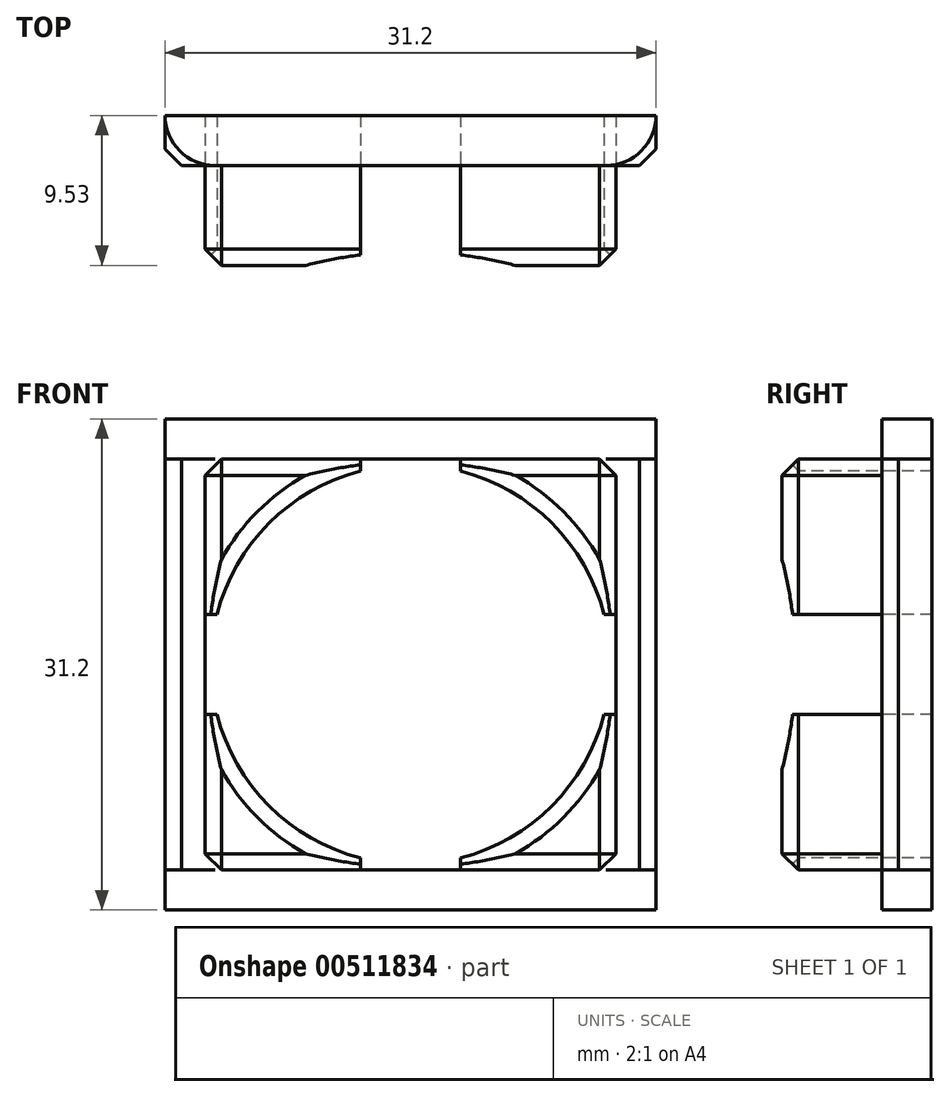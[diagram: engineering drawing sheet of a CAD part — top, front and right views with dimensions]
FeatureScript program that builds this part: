
annotation { "Feature Type Name" : "Feature", "Feature Type Description" : "" }
export const myFeature = defineFeature(function(context is Context, id is Id, definition is map)
    precondition{}
    {
        {
            var Q0;
            Q0=qCreatedBy(makeId("Front.planeOp"),FACE);
            var sketch = newSketch(context, id + "F0", { "sketchPlane" : qUnion([Q0])});
            skLineSegment(sketch, "E0.bottom", {"start": v(-15.6, 15.6) * mm, "end": v(15.6, 15.6) * mm});
            skLineSegment(sketch, "E0.top", {"start": v(-15.6, -15.6) * mm, "end": v(15.6, -15.6) * mm});
            skLineSegment(sketch, "E0.left", {"start": v(-15.6, 15.6) * mm, "end": v(-15.6, -15.6) * mm});
            skLineSegment(sketch, "E0.right", {"start": v(15.6, 15.6) * mm, "end": v(15.6, -15.6) * mm});
            skLineSegment(sketch, "E1", {"start": v(-15.6, 15.6) * mm, "end": v(15.6, -15.6) * mm, "construction": true});
            skLineSegment(sketch, "E2.0", {"start": v(-13.06, 13.06) * mm, "end": v(13.06, 13.06) * mm});
            skLineSegment(sketch, "E2.1", {"start": v(-13.06, 13.06) * mm, "end": v(-13.06, -13.06) * mm});
            skLineSegment(sketch, "E2.2", {"start": v(-13.06, -13.06) * mm, "end": v(13.06, -13.06) * mm});
            skLineSegment(sketch, "E2.3", {"start": v(13.06, 13.06) * mm, "end": v(13.06, -13.06) * mm});
            skCircle(sketch, "E3", {"center": v(0, 0) * mm, "radius": 12.7 * mm});
            skLineSegment(sketch, "E4", {"start": v(0, 13.06) * mm, "end": v(0, -13.06) * mm, "construction": true});
            skLineSegment(sketch, "E5", {"start": v(13.06, 0) * mm, "end": v(-13.06, 0) * mm, "construction": true});
            skLineSegment(sketch, "E6.0", {"start": v(-3.17, 13.06) * mm, "end": v(-3.17, -13.06) * mm});
            skLineSegment(sketch, "E7.MirrorCS", {"start": v(3.17, 13.06) * mm, "end": v(3.17, -13.06) * mm});
            skLineSegment(sketch, "E8.0", {"start": v(13.06, 3.18) * mm, "end": v(-13.06, 3.17) * mm});
            skLineSegment(sketch, "E9.MirrorCS", {"start": v(13.06, -3.18) * mm, "end": v(-13.06, -3.18) * mm});
            skSolve(sketch);
        }
        {
            var Q0;
            Q0=makeQuery(id+"F0.imprint","IMPRINT",FACE,{"disambiguationData":[TD([[makeQuery(id+"F0.imprint","IMPRINT",EDGE,{"derivedFrom":sQuery(id+"F0.wireOp",EDGE,"E0.bottom")}),-1.0]])]});
            var Q1;
            {var subQ0=sQuery(id+"F0.wireOp",EDGE,"E2.3");var subQ1=sQuery(id+"F0.wireOp",EDGE,"E2.0");var subQ2=makeQuery(id+"F0.imprint","INTERSECT",VERTEX,{"derivedFrom":[subQ1,subQ0]});Q1=makeQuery(id+"F0.imprint","IMPRINT",FACE,{"disambiguationData":[TD([[makeQuery(id+"F0.imprint","IMPRINT",EDGE,{"disambiguationData":[TD([[subQ2,1.0]])],"derivedFrom":subQ1}),-1.0]])]});}
            var Q2;
            {var subQ0=sQuery(id+"F0.wireOp",EDGE,"E2.1");var subQ1=sQuery(id+"F0.wireOp",EDGE,"E2.0");var subQ2=makeQuery(id+"F0.imprint","INTERSECT",VERTEX,{"derivedFrom":[subQ1,subQ0]});Q2=makeQuery(id+"F0.imprint","IMPRINT",FACE,{"disambiguationData":[TD([[makeQuery(id+"F0.imprint","IMPRINT",EDGE,{"disambiguationData":[TD([[subQ2,-1.0]])],"derivedFrom":subQ1}),-1.0]])]});}
            var Q3;
            {var subQ0=sQuery(id+"F0.wireOp",EDGE,"E2.2");var subQ1=sQuery(id+"F0.wireOp",EDGE,"E2.1");var subQ2=makeQuery(id+"F0.imprint","INTERSECT",VERTEX,{"derivedFrom":[subQ1,subQ0]});Q3=makeQuery(id+"F0.imprint","IMPRINT",FACE,{"disambiguationData":[TD([[makeQuery(id+"F0.imprint","IMPRINT",EDGE,{"disambiguationData":[TD([[subQ2,1.0]])],"derivedFrom":subQ1}),1.0]])]});}
            var Q4;
            {var subQ0=sQuery(id+"F0.wireOp",EDGE,"E2.3");var subQ1=sQuery(id+"F0.wireOp",EDGE,"E2.2");var subQ2=makeQuery(id+"F0.imprint","INTERSECT",VERTEX,{"derivedFrom":[subQ1,subQ0]});Q4=makeQuery(id+"F0.imprint","IMPRINT",FACE,{"disambiguationData":[TD([[makeQuery(id+"F0.imprint","IMPRINT",EDGE,{"disambiguationData":[TD([[subQ2,1.0]])],"derivedFrom":subQ1}),1.0]])]});}
            extrude(context, id + "F1", {"entities" : qUnion([Q0, Q1, Q2, Q3, Q4]), "oppositeDirection" : true, "depth" : 3.17 * mm, "offsetDistance" : 25.4 * mm});
        }
        {
            var Q0;
            {var subQ0=sQuery(id+"F0.wireOp",EDGE,"E2.2");var subQ1=sQuery(id+"F0.wireOp",EDGE,"E2.1");var subQ2=makeQuery(id+"F0.imprint","INTERSECT",VERTEX,{"derivedFrom":[subQ1,subQ0]});Q0=makeQuery(id+"F0.imprint","IMPRINT",FACE,{"disambiguationData":[TD([[makeQuery(id+"F0.imprint","IMPRINT",EDGE,{"disambiguationData":[TD([[subQ2,1.0]])],"derivedFrom":subQ1}),1.0]])]});}
            var Q1;
            {var subQ0=sQuery(id+"F0.wireOp",EDGE,"E2.3");var subQ1=sQuery(id+"F0.wireOp",EDGE,"E2.0");var subQ2=makeQuery(id+"F0.imprint","INTERSECT",VERTEX,{"derivedFrom":[subQ1,subQ0]});Q1=makeQuery(id+"F0.imprint","IMPRINT",FACE,{"disambiguationData":[TD([[makeQuery(id+"F0.imprint","IMPRINT",EDGE,{"disambiguationData":[TD([[subQ2,1.0]])],"derivedFrom":subQ1}),-1.0]])]});}
            var Q2;
            {var subQ0=sQuery(id+"F0.wireOp",EDGE,"E2.3");var subQ1=sQuery(id+"F0.wireOp",EDGE,"E2.2");var subQ2=makeQuery(id+"F0.imprint","INTERSECT",VERTEX,{"derivedFrom":[subQ1,subQ0]});Q2=makeQuery(id+"F0.imprint","IMPRINT",FACE,{"disambiguationData":[TD([[makeQuery(id+"F0.imprint","IMPRINT",EDGE,{"disambiguationData":[TD([[subQ2,1.0]])],"derivedFrom":subQ1}),1.0]])]});}
            var Q3;
            {var subQ0=sQuery(id+"F0.wireOp",EDGE,"E2.1");var subQ1=sQuery(id+"F0.wireOp",EDGE,"E2.0");var subQ2=makeQuery(id+"F0.imprint","INTERSECT",VERTEX,{"derivedFrom":[subQ1,subQ0]});Q3=makeQuery(id+"F0.imprint","IMPRINT",FACE,{"disambiguationData":[TD([[makeQuery(id+"F0.imprint","IMPRINT",EDGE,{"disambiguationData":[TD([[subQ2,-1.0]])],"derivedFrom":subQ1}),-1.0]])]});}
            extrude(context, id + "F2", {"entities" : qUnion([Q0, Q1, Q2, Q3]), "operationType" : NewBodyOperationType.ADD, "depth" : 6.35 * mm, "offsetDistance" : 25.4 * mm});
        }
        {
            var Q0;
            Q0=makeQuery(id+"F1.opExtrude","SWEPT_FACE",FACE,{"disambiguationData":[OSD([sQuery(id+"F0.wireOp",EDGE,"E0.top")])]});
            var sketch = newSketch(context, id + "F3", { "sketchPlane" : qUnion([Q0])});
            skLineSegment(sketch, "E10.bottom", {"start": v(-12.42, 0) * mm, "end": v(12.42, 0) * mm});
            skLineSegment(sketch, "E10.top", {"start": v(-15.6, -3.18) * mm, "end": v(15.6, -3.18) * mm});
            skLineSegment(sketch, "E10.left", {"start": v(-15.6, -3.18) * mm, "end": v(-15.6, -3.18) * mm});
            skLineSegment(sketch, "E10.right", {"start": v(15.6, -3.18) * mm, "end": v(15.6, -3.18) * mm});
            skPoint(sketch, "E11.visualSharp", {"position": v(-15.6, 0) * mm});
            skArc(sketch, "E11.filletArc", {"start": v(-12.42, 0) * mm, "mid": v(-14.67, -0.93) * mm, "end": v(-15.6, -3.18) * mm});
            skPoint(sketch, "E12.visualSharp", {"position": v(15.6, 0) * mm});
            skArc(sketch, "E12.filletArc", {"start": v(15.6, -3.18) * mm, "mid": v(14.67, -0.93) * mm, "end": v(12.42, 0) * mm});
            skSolve(sketch);
        }
        {
            var Q0;
            {var subQ0=sQuery(id+"F3.wireOp",EDGE,"E11.filletArc");Q0=makeQuery(id+"F3.imprint","IMPRINT",FACE,{"disambiguationData":[TD([[makeQuery(id+"F3.imprint","IMPRINT",EDGE,{"derivedFrom":subQ0}),-1.0]])]});}
            var Q1;
            {var subQ0=sQuery(id+"F3.wireOp",EDGE,"E12.filletArc");Q1=makeQuery(id+"F3.imprint","IMPRINT",FACE,{"disambiguationData":[TD([[makeQuery(id+"F3.imprint","IMPRINT",EDGE,{"derivedFrom":subQ0}),-1.0]])]});}
            var Q2;
            {var subQ0=sQuery(id+"F0.wireOp",EDGE,"E2.2");Q2=makeQuery(id+"F2.opExtrude","SWEPT_FACE",FACE,{"disambiguationData":[OSD([subQ0]),TDD([makeQuery(id+"F0.imprint","IMPRINT",EDGE,{"disambiguationData":[TD([[makeQuery(id+"F0.imprint","INTERSECT",VERTEX,{"derivedFrom":[sQuery(id+"F0.wireOp",EDGE,"E2.1"),subQ0]}),-1.0]])],"derivedFrom":subQ0})])]});}
            extrude(context, id + "F4", {"entities" : qUnion([Q0, Q1]), "operationType" : NewBodyOperationType.REMOVE, "endBound" : BoundingType.UP_TO_SURFACE, "oppositeDirection" : true, "depth" : 3.17 * mm, "endBoundEntityFace" : qUnion([Q2]), "offsetDistance" : 25.4 * mm});
        }
        {
            var Q0;
            Q0=makeQuery(id+"F1.opExtrude","SWEPT_FACE",FACE,{"disambiguationData":[OSD([sQuery(id+"F0.wireOp",EDGE,"E0.bottom")])]});
            var sketch = newSketch(context, id + "F5", { "sketchPlane" : qUnion([Q0])});
            skLineSegment(sketch, "E13.bottom", {"start": v(12.42, 0) * mm, "end": v(-12.42, 0) * mm});
            skLineSegment(sketch, "E13.top", {"start": v(15.6, 3.18) * mm, "end": v(-15.6, 3.18) * mm});
            skLineSegment(sketch, "E13.left", {"start": v(15.6, 3.18) * mm, "end": v(15.6, 3.18) * mm});
            skLineSegment(sketch, "E13.right", {"start": v(-15.6, 3.17) * mm, "end": v(-15.6, 3.18) * mm});
            skPoint(sketch, "E14.visualSharp", {"position": v(15.6, 0) * mm});
            skArc(sketch, "E14.filletArc", {"start": v(12.42, 0) * mm, "mid": v(14.67, 0.93) * mm, "end": v(15.6, 3.18) * mm});
            skPoint(sketch, "E15.visualSharp", {"position": v(-15.6, 0) * mm});
            skArc(sketch, "E15.filletArc", {"start": v(-15.6, 3.17) * mm, "mid": v(-14.67, 0.93) * mm, "end": v(-12.42, 0) * mm});
            skSolve(sketch);
        }
        {
            var Q0;
            {var subQ0=sQuery(id+"F5.wireOp",EDGE,"E14.filletArc");Q0=makeQuery(id+"F5.imprint","IMPRINT",FACE,{"disambiguationData":[TD([[makeQuery(id+"F5.imprint","IMPRINT",EDGE,{"derivedFrom":subQ0}),-1.0]])]});}
            var Q1;
            {var subQ0=sQuery(id+"F5.wireOp",EDGE,"E15.filletArc");Q1=makeQuery(id+"F5.imprint","IMPRINT",FACE,{"disambiguationData":[TD([[makeQuery(id+"F5.imprint","IMPRINT",EDGE,{"derivedFrom":subQ0}),-1.0]])]});}
            var Q2;
            {var subQ0=sQuery(id+"F0.wireOp",EDGE,"E2.0");Q2=makeQuery(id+"F2.opExtrude","SWEPT_FACE",FACE,{"disambiguationData":[OSD([subQ0]),TDD([makeQuery(id+"F0.imprint","IMPRINT",EDGE,{"disambiguationData":[TD([[makeQuery(id+"F0.imprint","INTERSECT",VERTEX,{"derivedFrom":[subQ0,sQuery(id+"F0.wireOp",EDGE,"E2.3")]}),1.0]])],"derivedFrom":subQ0})])]});}
            extrude(context, id + "F6", {"entities" : qUnion([Q0, Q1]), "operationType" : NewBodyOperationType.REMOVE, "endBound" : BoundingType.UP_TO_SURFACE, "oppositeDirection" : true, "depth" : 25.4 * mm, "endBoundEntityFace" : qUnion([Q2]), "offsetDistance" : 25.4 * mm});
        }
        {
            var Q0;
            Q0=makeQuery(id+"F2.opExtrude","CAP_FACE",FACE,{"disambiguationData":[OSD([sQuery(id+"F0.wireOp",EDGE,"E2.0"),sQuery(id+"F0.wireOp",EDGE,"E2.1"),sQuery(id+"F0.wireOp",EDGE,"E3"),sQuery(id+"F0.wireOp",EDGE,"E6.0"),sQuery(id+"F0.wireOp",EDGE,"E8.0")])],"isStart":false});
            var Q1;
            Q1=makeQuery(id+"F2.opExtrude","CAP_FACE",FACE,{"disambiguationData":[OSD([sQuery(id+"F0.wireOp",EDGE,"E2.0"),sQuery(id+"F0.wireOp",EDGE,"E2.3"),sQuery(id+"F0.wireOp",EDGE,"E3"),sQuery(id+"F0.wireOp",EDGE,"E7.MirrorCS"),sQuery(id+"F0.wireOp",EDGE,"E8.0")])],"isStart":false});
            var Q2;
            Q2=makeQuery(id+"F2.opExtrude","CAP_FACE",FACE,{"disambiguationData":[OSD([sQuery(id+"F0.wireOp",EDGE,"E2.2"),sQuery(id+"F0.wireOp",EDGE,"E2.3"),sQuery(id+"F0.wireOp",EDGE,"E3"),sQuery(id+"F0.wireOp",EDGE,"E7.MirrorCS"),sQuery(id+"F0.wireOp",EDGE,"E9.MirrorCS")])],"isStart":false});
            var Q3;
            Q3=makeQuery(id+"F2.opExtrude","CAP_FACE",FACE,{"disambiguationData":[OSD([sQuery(id+"F0.wireOp",EDGE,"E2.1"),sQuery(id+"F0.wireOp",EDGE,"E2.2"),sQuery(id+"F0.wireOp",EDGE,"E3"),sQuery(id+"F0.wireOp",EDGE,"E6.0"),sQuery(id+"F0.wireOp",EDGE,"E9.MirrorCS")])],"isStart":false});
            var Q4;
            Q4=makeQuery(id+"F2.opExtrude","SWEPT_EDGE",EDGE,{"disambiguationData":[OSD([sQuery(id+"F0.wireOp",EDGE,"E2.1"),sQuery(id+"F0.wireOp",EDGE,"E2.2")])]});
            var Q5;
            Q5=makeQuery(id+"F2.opExtrude","SWEPT_EDGE",EDGE,{"disambiguationData":[OSD([sQuery(id+"F0.wireOp",EDGE,"E2.2"),sQuery(id+"F0.wireOp",EDGE,"E2.3")])]});
            var Q6;
            Q6=makeQuery(id+"F2.opExtrude","SWEPT_EDGE",EDGE,{"disambiguationData":[OSD([sQuery(id+"F0.wireOp",EDGE,"E2.0"),sQuery(id+"F0.wireOp",EDGE,"E2.1")])]});
            var Q7;
            Q7=makeQuery(id+"F2.opExtrude","SWEPT_EDGE",EDGE,{"disambiguationData":[OSD([sQuery(id+"F0.wireOp",EDGE,"E2.0"),sQuery(id+"F0.wireOp",EDGE,"E2.3")])]});
            var Q8;
            Q8=makeQuery(id+"F1.opExtrude","CAP_EDGE",EDGE,{"disambiguationData":[OSD([sQuery(id+"F0.wireOp",EDGE,"E0.left")])],"isStart":true});
            var Q9;
            Q9=makeQuery(id+"F1.opExtrude","CAP_EDGE",EDGE,{"disambiguationData":[OSD([sQuery(id+"F0.wireOp",EDGE,"E0.right")])],"isStart":true});
            chamfer(context, id + "F7", {"entities" : qUnion([Q0, Q1, Q2, Q3, Q4, Q5, Q6, Q7, Q8, Q9]), "width" : 1.04 * mm, "tangentPropagation" : true});
        }
    });
